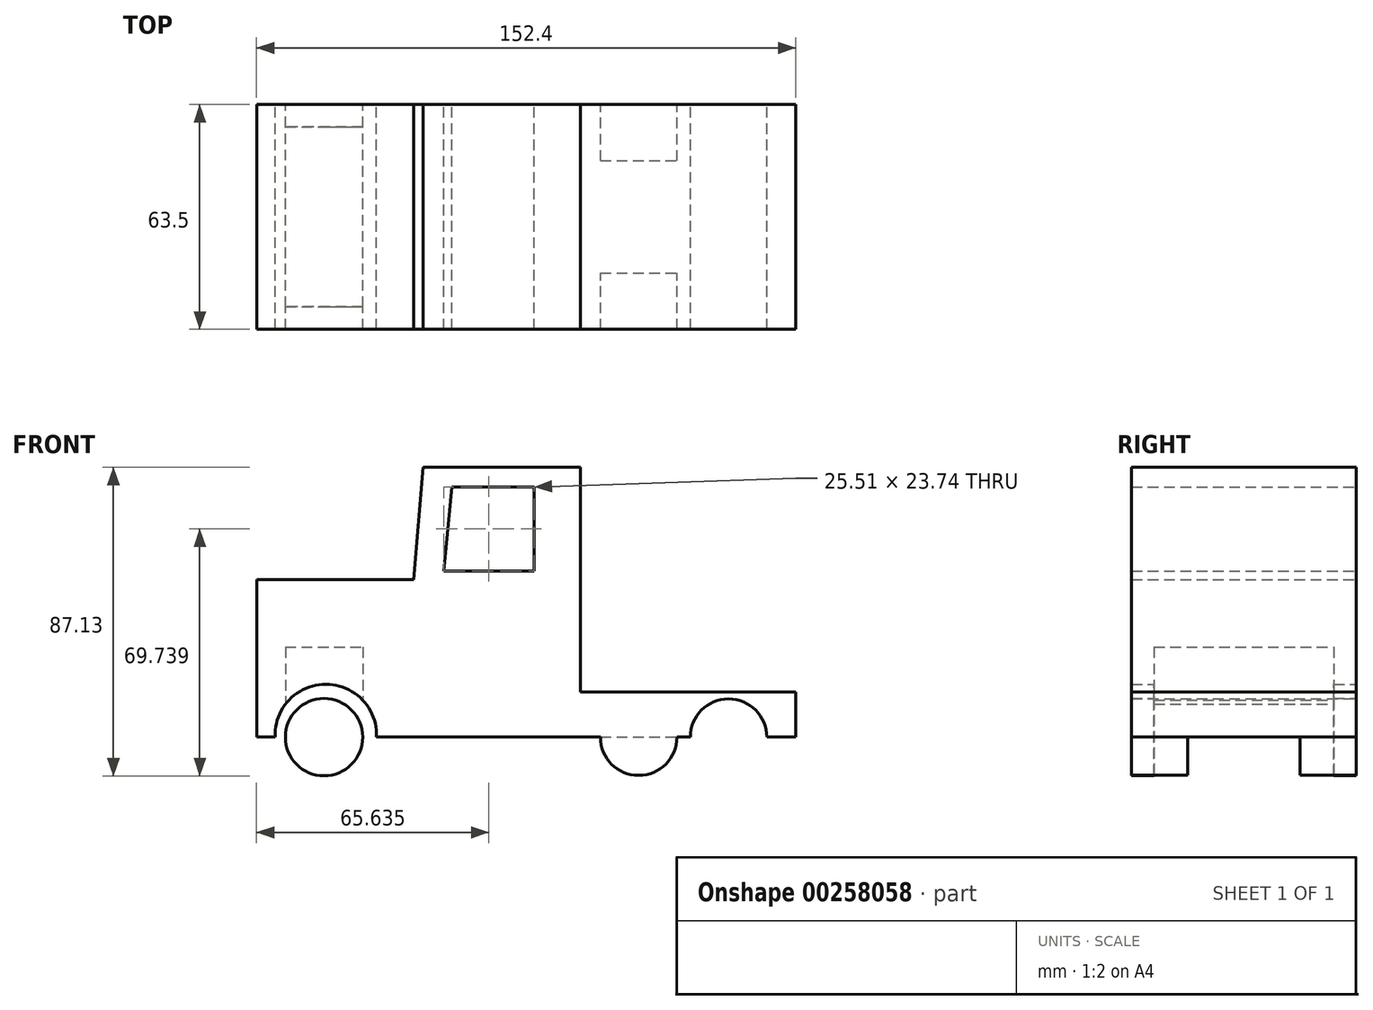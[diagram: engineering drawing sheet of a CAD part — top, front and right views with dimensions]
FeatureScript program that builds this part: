
annotation { "Feature Type Name" : "Feature", "Feature Type Description" : "" }
export const myFeature = defineFeature(function(context is Context, id is Id, definition is map)
    precondition{}
    {
        {
            var Q0;
            Q0=qCreatedBy(makeId("Front.planeOp"),FACE);
            var sketch = newSketch(context, id + "F0", { "sketchPlane" : qUnion([Q0])});
            skLineSegment(sketch, "E0", {"start": v(-50.66, -17.11) * mm, "end": v(101.74, -17.11) * mm});
            skLineSegment(sketch, "E1", {"start": v(101.74, -4.41) * mm, "end": v(40.78, -4.41) * mm});
            skLineSegment(sketch, "E2", {"start": v(40.78, -4.41) * mm, "end": v(40.78, 59.09) * mm});
            skLineSegment(sketch, "E3", {"start": v(40.78, 59.09) * mm, "end": v(-3.67, 59.09) * mm});
            skLineSegment(sketch, "E4", {"start": v(-3.67, 59.09) * mm, "end": v(-6.2, 27.34) * mm});
            skLineSegment(sketch, "E5", {"start": v(-6.2, 27.34) * mm, "end": v(-50.66, 27.34) * mm});
            skLineSegment(sketch, "E6", {"start": v(-50.66, 27.34) * mm, "end": v(-50.66, -17.11) * mm});
            skCircle(sketch, "E7", {"center": v(-31.6, -17.11) * mm, "radius": 10.92 * mm});
            skCircle(sketch, "E8", {"center": v(57.3, -17.11) * mm, "radius": 10.8 * mm});
            skCircle(sketch, "E9", {"center": v(82.7, -17.11) * mm, "radius": 10.8 * mm});
            skLineSegment(sketch, "E10", {"start": v(101.74, -17.11) * mm, "end": v(101.74, -4.41) * mm});
            skArc(sketch, "E11", {"start": v(-16.76, -17.11) * mm, "mid": v(-31.09, -2.15) * mm, "end": v(-45.42, -17.11) * mm});
            skLineSegment(sketch, "E12", {"start": v(65.53, -4.41) * mm, "end": v(65.53, 0) * mm});
            skLineSegment(sketch, "E13", {"start": v(65.53, 0) * mm, "end": v(69.8, 0) * mm});
            skLineSegment(sketch, "E14", {"start": v(69.8, 0) * mm, "end": v(69.8, -4.41) * mm});
            skLineSegment(sketch, "E15", {"start": v(61.57, 0) * mm, "end": v(79.55, 0) * mm});
            skLineSegment(sketch, "E16", {"start": v(61.57, 4.88) * mm, "end": v(61.57, 0) * mm});
            skLineSegment(sketch, "E17", {"start": v(79.55, 0) * mm, "end": v(79.55, 2.3) * mm});
            skLineSegment(sketch, "E18", {"start": v(79.55, 2.3) * mm, "end": v(61.57, 4.88) * mm});
            skLineSegment(sketch, "E19", {"start": v(2.22, 29.83) * mm, "end": v(4.5, 53.57) * mm});
            skLineSegment(sketch, "E20", {"start": v(4.5, 53.57) * mm, "end": v(27.72, 53.57) * mm});
            skLineSegment(sketch, "E21", {"start": v(27.73, 29.83) * mm, "end": v(2.22, 29.83) * mm});
            skLineSegment(sketch, "E22", {"start": v(27.73, 29.83) * mm, "end": v(27.72, 53.57) * mm});
            skSolve(sketch);
        }
        {
            var Q0;
            {var subQ0=sQuery(id+"F0.wireOp",EDGE,"E2");Q0=makeQuery(id+"F0.imprint","IMPRINT",FACE,{"disambiguationData":[TD([[makeQuery(id+"F0.imprint","IMPRINT",EDGE,{"derivedFrom":subQ0}),1.0]])]});}
            var Q1;
            {var subQ0=sQuery(id+"F0.wireOp",EDGE,"E8");var subQ1=sQuery(id+"F0.wireOp",EDGE,"E0");var subQ2=makeQuery(id+"F0.imprint","INTERSECT",VERTEX,{"disambiguationData":[OD(0.0)],"derivedFrom":[subQ1,subQ0]});Q1=makeQuery(id+"F0.imprint","IMPRINT",FACE,{"disambiguationData":[TD([[makeQuery(id+"F0.imprint","IMPRINT",EDGE,{"disambiguationData":[TD([[subQ2,-1.0]])],"derivedFrom":subQ1}),1.0]])]});}
            var Q2;
            {var subQ0=sQuery(id+"F0.wireOp",EDGE,"E9");var subQ1=sQuery(id+"F0.wireOp",EDGE,"E0");var subQ2=makeQuery(id+"F0.imprint","INTERSECT",VERTEX,{"disambiguationData":[OD(0.0)],"derivedFrom":[subQ1,subQ0]});Q2=makeQuery(id+"F0.imprint","IMPRINT",FACE,{"disambiguationData":[TD([[makeQuery(id+"F0.imprint","IMPRINT",EDGE,{"disambiguationData":[TD([[subQ2,-1.0]])],"derivedFrom":subQ1}),1.0]])]});}
            extrude(context, id + "F1", {"entities" : qUnion([Q0, Q1, Q2]), "endBound" : BoundingType.SYMMETRIC, "depth" : 63.5 * mm});
        }
        {
            var Q0;
            {var subQ0=sQuery(id+"F0.wireOp",EDGE,"E7");var subQ1=sQuery(id+"F0.wireOp",EDGE,"E0");var subQ2=makeQuery(id+"F0.imprint","INTERSECT",VERTEX,{"disambiguationData":[OD(0.0)],"derivedFrom":[subQ1,subQ0]});Q0=makeQuery(id+"F0.imprint","IMPRINT",FACE,{"disambiguationData":[TD([[makeQuery(id+"F0.imprint","IMPRINT",EDGE,{"disambiguationData":[TD([[subQ2,-1.0]])],"derivedFrom":subQ1}),1.0]])]});}
            var Q1;
            {var subQ0=sQuery(id+"F0.wireOp",EDGE,"E7");var subQ1=sQuery(id+"F0.wireOp",EDGE,"E0");var subQ2=makeQuery(id+"F0.imprint","INTERSECT",VERTEX,{"disambiguationData":[OD(0.0)],"derivedFrom":[subQ1,subQ0]});Q1=makeQuery(id+"F0.imprint","IMPRINT",FACE,{"disambiguationData":[TD([[makeQuery(id+"F0.imprint","IMPRINT",EDGE,{"disambiguationData":[TD([[subQ2,-1.0]])],"derivedFrom":subQ1}),-1.0]])]});}
            var Q2;
            {var subQ0=sQuery(id+"F0.wireOp",EDGE,"E8");var subQ1=sQuery(id+"F0.wireOp",EDGE,"E0");var subQ2=makeQuery(id+"F0.imprint","INTERSECT",VERTEX,{"disambiguationData":[OD(0.0)],"derivedFrom":[subQ1,subQ0]});Q2=makeQuery(id+"F0.imprint","IMPRINT",FACE,{"disambiguationData":[TD([[makeQuery(id+"F0.imprint","IMPRINT",EDGE,{"disambiguationData":[TD([[subQ2,-1.0]])],"derivedFrom":subQ1}),-1.0]])]});}
            var Q3;
            {var subQ0=sQuery(id+"F0.wireOp",EDGE,"E9");var subQ1=sQuery(id+"F0.wireOp",EDGE,"E0");var subQ2=makeQuery(id+"F0.imprint","INTERSECT",VERTEX,{"disambiguationData":[OD(0.0)],"derivedFrom":[subQ1,subQ0]});Q3=makeQuery(id+"F0.imprint","IMPRINT",FACE,{"disambiguationData":[TD([[makeQuery(id+"F0.imprint","IMPRINT",EDGE,{"disambiguationData":[TD([[subQ2,-1.0]])],"derivedFrom":subQ1}),-1.0]])]});}
            extrude(context, id + "F2", {"entities" : qUnion([Q0, Q1, Q2, Q3]), "operationType" : NewBodyOperationType.ADD, "endBound" : BoundingType.SYMMETRIC, "depth" : 63.5 * mm});
        }
        {
            var Q0;
            {var subQ0=sQuery(id+"F0.wireOp",EDGE,"E7");var subQ1=sQuery(id+"F0.wireOp",EDGE,"E0");var subQ2=makeQuery(id+"F0.imprint","INTERSECT",VERTEX,{"disambiguationData":[OD(0.0)],"derivedFrom":[subQ1,subQ0]});Q0=makeQuery(id+"F0.imprint","IMPRINT",FACE,{"disambiguationData":[TD([[makeQuery(id+"F0.imprint","IMPRINT",EDGE,{"disambiguationData":[TD([[subQ2,-1.0]])],"derivedFrom":subQ1}),-1.0]])]});}
            extrude(context, id + "F3", {"entities" : qUnion([Q0]), "operationType" : NewBodyOperationType.REMOVE, "endBound" : BoundingType.SYMMETRIC, "depth" : 50.8 * mm});
        }
        {
            var Q0;
            Q0=makeQuery(id+"F3.boolean.opBoolean","COPY",FACE,{"derivedFrom":makeQuery(id+"F3.opExtrude","SWEPT_FACE",FACE,{"disambiguationData":[OSD([sQuery(id+"F0.wireOp",EDGE,"E0")])]})});
            extrude(context, id + "F4", {"entities" : qUnion([Q0]), "operationType" : NewBodyOperationType.REMOVE, "oppositeDirection" : true, "depth" : 25.4 * mm});
        }
        {
            var Q0;
            {var subQ0=sQuery(id+"F0.wireOp",EDGE,"E9");var subQ1=sQuery(id+"F0.wireOp",EDGE,"E0");var subQ2=makeQuery(id+"F0.imprint","INTERSECT",VERTEX,{"disambiguationData":[OD(0.0)],"derivedFrom":[subQ1,subQ0]});Q0=makeQuery(id+"F0.imprint","IMPRINT",FACE,{"disambiguationData":[TD([[makeQuery(id+"F0.imprint","IMPRINT",EDGE,{"disambiguationData":[TD([[subQ2,-1.0]])],"derivedFrom":subQ1}),-1.0]])]});}
            var Q1;
            {var subQ0=sQuery(id+"F0.wireOp",EDGE,"E8");var subQ1=sQuery(id+"F0.wireOp",EDGE,"E0");var subQ2=makeQuery(id+"F0.imprint","INTERSECT",VERTEX,{"disambiguationData":[OD(0.0)],"derivedFrom":[subQ1,subQ0]});Q1=makeQuery(id+"F0.imprint","IMPRINT",FACE,{"disambiguationData":[TD([[makeQuery(id+"F0.imprint","IMPRINT",EDGE,{"disambiguationData":[TD([[subQ2,-1.0]])],"derivedFrom":subQ1}),-1.0]])]});}
            var Q2;
            Q2=sQuery(id+"F0.wireOp",EDGE,"E9");
            var Q3;
            Q3=sQuery(id+"F0.wireOp",EDGE,"E8");
            extrude(context, id + "F5", {"entities" : qUnion([Q0, Q1]), "operationType" : NewBodyOperationType.REMOVE, "surfaceEntities" : qUnion([Q2, Q3]), "endBound" : BoundingType.SYMMETRIC, "depth" : 31.75 * mm});
        }
        {
            var Q0;
            Q0=makeQuery(id+"F1.opExtrude","SWEPT_FACE",FACE,{"disambiguationData":[OSD([sQuery(id+"F0.wireOp",EDGE,"E4")])]});
            var sketch = newSketch(context, id + "F6", { "sketchPlane" : qUnion([Q0])});
            skLineSegment(sketch, "E23", {"start": v(-26.6, 53.52) * mm, "end": v(26.67, 53.52) * mm});
            skLineSegment(sketch, "E24", {"start": v(26.67, 53.52) * mm, "end": v(26.67, 31.83) * mm});
            skLineSegment(sketch, "E25", {"start": v(26.67, 31.83) * mm, "end": v(-26.67, 31.83) * mm});
            skLineSegment(sketch, "E26", {"start": v(-26.67, 31.83) * mm, "end": v(-26.6, 53.52) * mm});
            skSolve(sketch);
        }
        {
            var Q0;
            Q0=makeQuery(id+"F6.imprint","IMPRINT",FACE,{"disambiguationData":[TD([[makeQuery(id+"F6.imprint","IMPRINT",EDGE,{"derivedFrom":sQuery(id+"F6.wireOp",EDGE,"E23")}),-1.0]])]});
            extrude(context, id + "F7", {"entities" : qUnion([Q0]), "operationType" : NewBodyOperationType.REMOVE, "depth" : 25.4 * mm});
        }
    });
